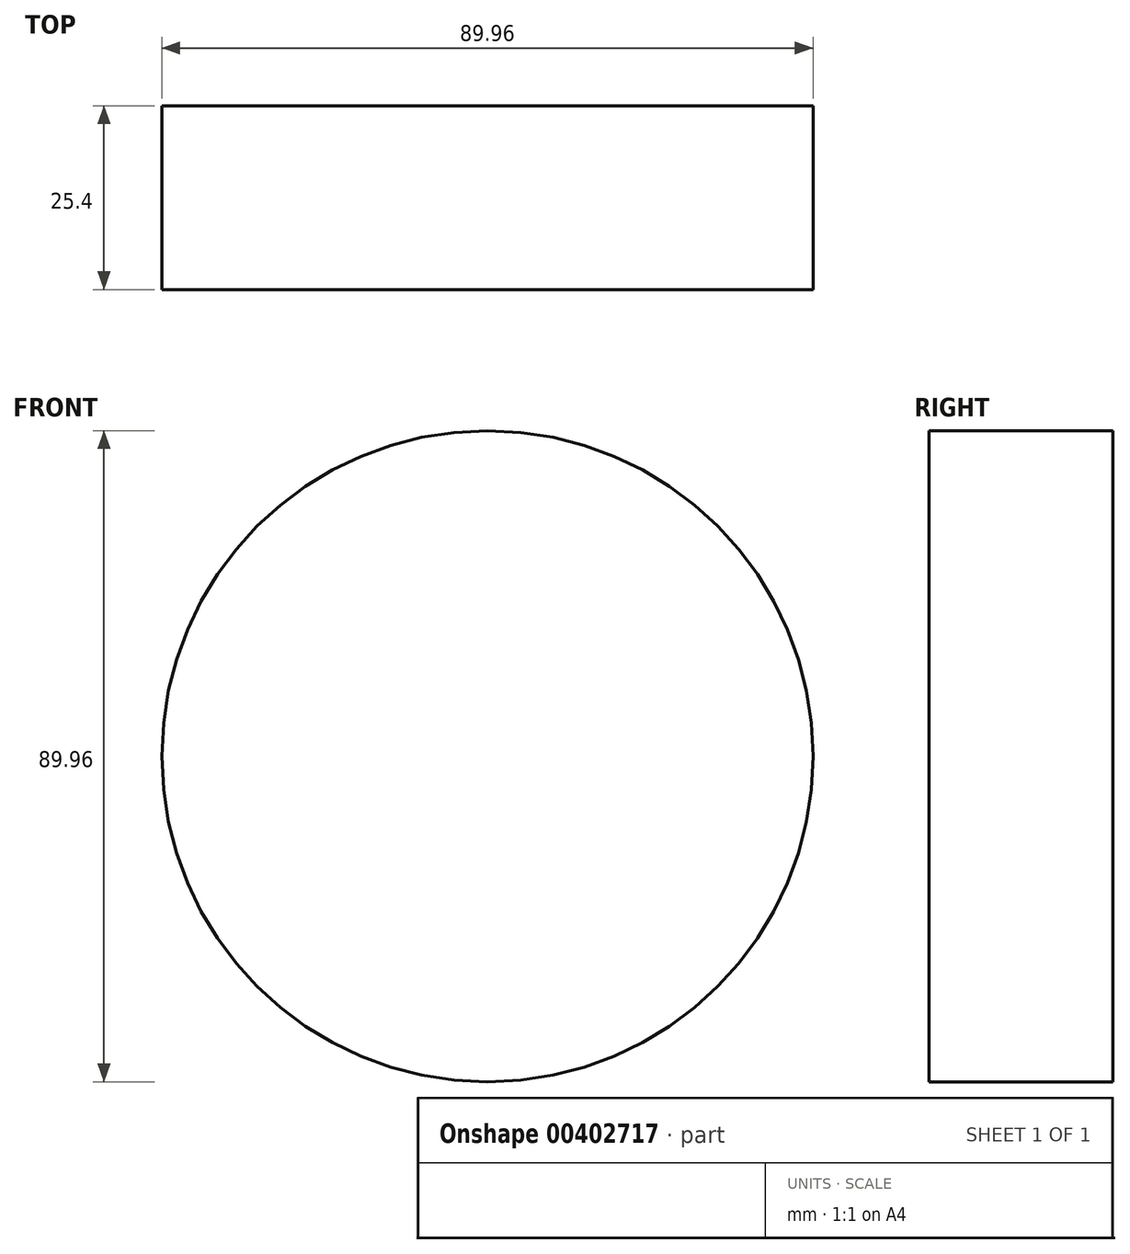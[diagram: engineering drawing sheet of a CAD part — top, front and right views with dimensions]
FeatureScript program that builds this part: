
annotation { "Feature Type Name" : "Feature", "Feature Type Description" : "" }
export const myFeature = defineFeature(function(context is Context, id is Id, definition is map)
    precondition{}
    {
        {
            var Q0;
            Q0=qCreatedBy(makeId("Front.planeOp"),FACE);
            var sketch = newSketch(context, id + "F0", { "sketchPlane" : qUnion([Q0])});
            skCircle(sketch, "E0", {"center": v(0, 0) * mm, "radius": 44.98 * mm});
            skSolve(sketch);
        }
        {
            var Q0;
            Q0=makeQuery(id+"F0.imprint","IMPRINT",FACE,{"disambiguationData":[TD([[makeQuery(id+"F0.imprint","IMPRINT",EDGE,{"derivedFrom":sQuery(id+"F0.wireOp",EDGE,"E0")}),1.0]])]});
            extrude(context, id + "F1", {"entities" : qUnion([Q0]), "depth" : 25.4 * mm});
        }
    });
